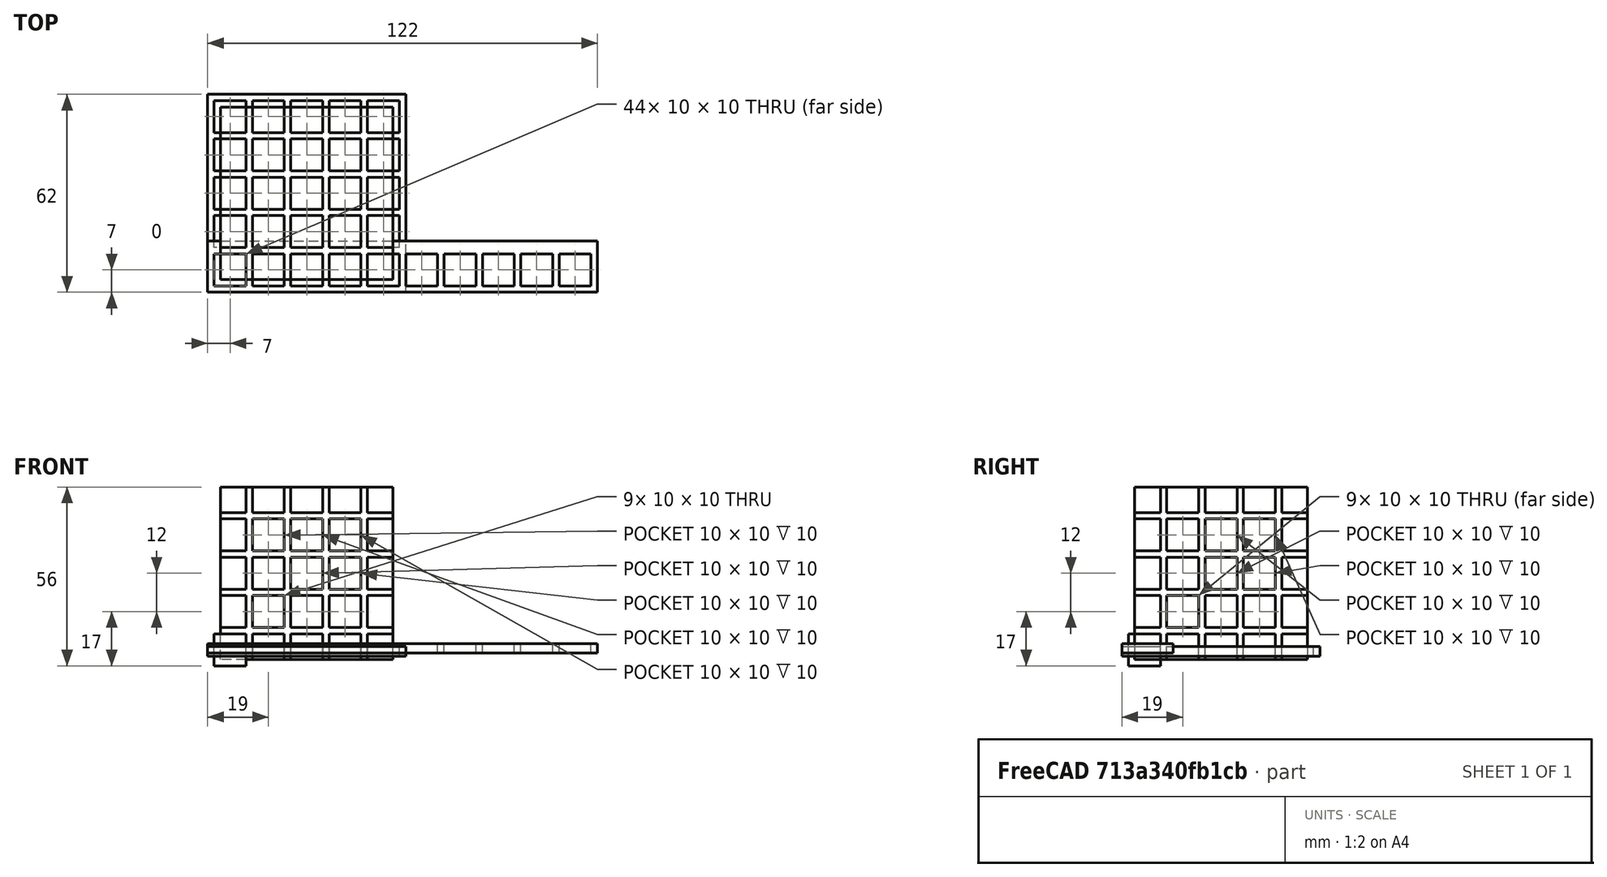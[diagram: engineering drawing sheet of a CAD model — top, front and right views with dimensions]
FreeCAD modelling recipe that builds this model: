
FCSTD DOCUMENT  (FreeCAD 0.21R33694 (Git))
Label: OJT1_T10P01_arrays
License: All rights reserved
LicenseURL: https://en.wikipedia.org/wiki/All_rights_reserved
objects: Part::Box×6, Part::FeaturePython×3, Part::Cut×3
note: 9 computed .brp shape members not serialized (recipe doc carries the construction recipe); baked Part::Feature solids carry a one-line shape summary decoded from their .brp

FEATURE [Part::Box] Box  label="Cub"
  AttacherType = Attacher::AttachEngine3D
  Height = 10
  Length = 10
  Width = 10
FEATURE [Part::FeaturePython] Array  # Draft array (typed FeaturePython)
  AlwaysSyncPlacement = false
  Angle = 360
  ArrayType = 0
  Axis = (0,0,1)
  Base = -> Box
  Center = (0,0,0)
  Count = 10
  ExpandArray = false
  Fuse = false
  IntervalAxis = (0,0,0)
  IntervalX = (12,0,0)
  IntervalY = (0,100,0)
  IntervalZ = (0,0,100)
  NumberCircles = 3
  NumberPolar = 5
  NumberX = 10
  NumberY = 1
  NumberZ = 1
  PlacementList = 10 placements: arithmetic series from (0,0,0) step (12,0,0) to (108,0,0)
  RadialDistance = 50
  ScaleList = (10) [(1,1,1),(1,1,1),(1,1,1),(1,1,1),(1,1,1),(1,1,1),(1,1,1),(1,1,1),(1,1,1),(1,1,1)]
  Symmetry = 1
  TangentialDistance = 25
FEATURE [Part::Box] Box001  label="Base"
  AttacherType = Attacher::AttachEngine3D
  Height = 3
  Length = 122
  Placement = pos=(-2,-2,4) rot=(0,0,1;0rad)
  Width = 16
FEATURE [Part::Cut] Cut
  Base = -> Box001
  Tool = -> Array
FEATURE [Part::Box] Box002  label="Master_box"
  AttacherType = Attacher::AttachEngine3D
  Height = 10
  Length = 10
  Width = 10
FEATURE [Part::FeaturePython] Array001  # Draft array (typed FeaturePython)
  AlwaysSyncPlacement = false
  Angle = 360
  ArrayType = 0
  Axis = (0,0,1)
  Base = -> Box002
  Center = (0,0,0)
  Count = 25
  ExpandArray = false
  Fuse = false
  IntervalAxis = (0,0,0)
  IntervalX = (12,0,0)
  IntervalY = (0,12,0)
  IntervalZ = (0,0,100)
  NumberCircles = 3
  NumberPolar = 5
  NumberX = 5
  NumberY = 5
  NumberZ = 1
  PlacementList = 25 placements: [(0,0,0),(0,12,0),(0,24,0),(0,36,0),(0,48,0),(12,0,0),(12,12,0),(12,24,0),(12,36,0),(12,48,0),(24,0,0),(24,12,0),(24,24,0),(24,36,0),(24,48,0),(36,0,0),(36,12,0),(36,24,0),(36,36,0),(36,48,0),(48,0,0),(48,12,0),(48,24,0),(48,36,0),(48,48,0)]
  RadialDistance = 50
  ScaleList = (25) [(1,1,1),(1,1,1),(1,1,1),(1,1,1),(1,1,1),(1,1,1),(1,1,1),(1,1,1),(1,1,1),(1,1,1),(1,1,1),(1,1,1),(1,1,1),(1,1,1),(1,1,1),(1,1,1),(1,1,1),(1,1,1),+7 more]
  Symmetry = 1
  TangentialDistance = 25
FEATURE [Part::Box] Box003  label="Cub001"
  AttacherType = Attacher::AttachEngine3D
  Height = 3
  Length = 62
  Placement = pos=(-2,-2,3) rot=(0,0,1;0rad)
  Width = 62
FEATURE [Part::Cut] Cut001
  Base = -> Box003
  Tool = -> Array001
FEATURE [Part::Box] Box004  label="Cub002"
  AttacherType = Attacher::AttachEngine3D
  Height = 10
  Length = 10
  Width = 10
FEATURE [Part::FeaturePython] Array002  # Draft array (typed FeaturePython)
  AlwaysSyncPlacement = false
  Angle = 360
  ArrayType = 0
  Axis = (0,0,1)
  Base = -> Box004
  Center = (0,0,0)
  Count = 125
  ExpandArray = false
  Fuse = false
  IntervalAxis = (0,0,0)
  IntervalX = (12,0,0)
  IntervalY = (0,12,0)
  IntervalZ = (0,0,12)
  NumberCircles = 3
  NumberPolar = 5
  NumberX = 5
  NumberY = 5
  NumberZ = 5
  PlacementList = 125 placements: [(0,0,0),(0,0,12),(0,0,24),(0,0,36),(0,0,48),(0,12,0),(0,12,12),(0,12,24),(0,12,36),(0,12,48),(0,24,0),(0,24,12),(0,24,24),(0,24,36),(0,24,48),(0,36,0),(0,36,12),(0,36,24),(0,36,36),(0,36,48),(0,48,0),(0,48,12),(0,48,24),(0,48,36),(0,48,48),(12,0,0),(12,0,12),(12,0,24),(12,0,36),(12,0,48),(12,12,0),(12,12,12),(12,12,24),(12,12,36),(12,12,48),(12,24,0),(12,24,12),(12,24,24),(12,24,36),(12,24,48),+85 more]
  RadialDistance = 50
  ScaleList = (125) [(1,1,1),(1,1,1),(1,1,1),(1,1,1),(1,1,1),(1,1,1),(1,1,1),(1,1,1),(1,1,1),(1,1,1),(1,1,1),(1,1,1),(1,1,1),(1,1,1),(1,1,1),(1,1,1),(1,1,1),(1,1,1),+107 more]
  Symmetry = 1
  TangentialDistance = 25
FEATURE [Part::Box] Box005  label="Cub003"
  AttacherType = Attacher::AttachEngine3D
  Height = 54
  Length = 54
  Placement = pos=(2,2,2) rot=(0,0,1;0rad)
  Width = 54
FEATURE [Part::Cut] Cut002
  Base = -> Box005
  Tool = -> Array002
